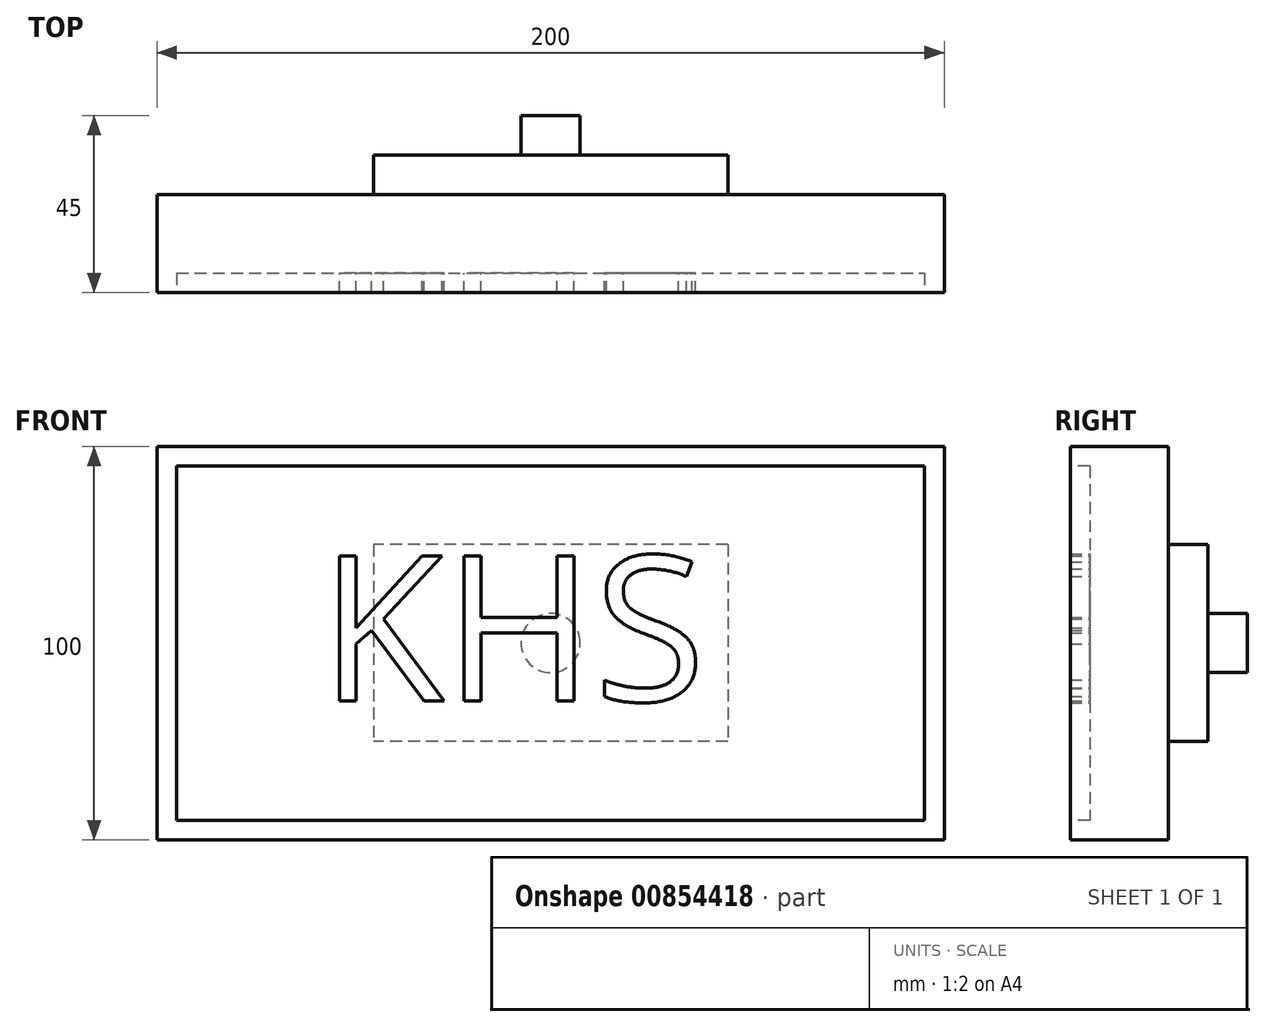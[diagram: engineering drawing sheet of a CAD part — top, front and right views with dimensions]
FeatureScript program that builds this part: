
annotation { "Feature Type Name" : "Feature", "Feature Type Description" : "" }
export const myFeature = defineFeature(function(context is Context, id is Id, definition is map)
    precondition{}
    {
        {
            var Q0;
            Q0=qCreatedBy(makeId("Front.planeOp"),FACE);
            var sketch = newSketch(context, id + "F0", { "sketchPlane" : qUnion([Q0])});
            skLineSegment(sketch, "E0.bottom", {"start": v(-100, 50) * mm, "end": v(100, 50) * mm});
            skLineSegment(sketch, "E0.top", {"start": v(-100, -50) * mm, "end": v(100, -50) * mm});
            skLineSegment(sketch, "E0.left", {"start": v(-100, 50) * mm, "end": v(-100, -50) * mm});
            skLineSegment(sketch, "E0.right", {"start": v(100, 50) * mm, "end": v(100, -50) * mm});
            skSolve(sketch);
        }
        {
            var Q0;
            Q0=makeQuery(id+"F0.imprint","IMPRINT",FACE,{"disambiguationData":[TD([[makeQuery(id+"F0.imprint","IMPRINT",EDGE,{"derivedFrom":sQuery(id+"F0.wireOp",EDGE,"E0.bottom")}),-1.0]])]});
            extrude(context, id + "F1", {"entities" : qUnion([Q0]), "depth" : 25 * mm, "offsetDistance" : 25 * mm});
        }
        {
            var Q0;
            Q0=makeQuery(id+"F1.opExtrude","CAP_FACE",FACE,{"disambiguationData":[OSD([sQuery(id+"F0.wireOp",EDGE,"E0.bottom"),sQuery(id+"F0.wireOp",EDGE,"E0.top"),sQuery(id+"F0.wireOp",EDGE,"E0.left"),sQuery(id+"F0.wireOp",EDGE,"E0.right")])],"isStart":false});
            var sketch = newSketch(context, id + "F2", { "sketchPlane" : qUnion([Q0])});
            skLineSegment(sketch, "E1.bottom", {"start": v(-95, 45) * mm, "end": v(95, 45) * mm});
            skLineSegment(sketch, "E1.top", {"start": v(-95, -45) * mm, "end": v(95, -45) * mm});
            skLineSegment(sketch, "E1.left", {"start": v(-95, 45) * mm, "end": v(-95, -45) * mm});
            skLineSegment(sketch, "E1.right", {"start": v(95, 45) * mm, "end": v(95, -45) * mm});
            skSolve(sketch);
        }
        {
            var Q0;
            Q0=makeQuery(id+"F2.imprint","IMPRINT",FACE,{"disambiguationData":[TD([[makeQuery(id+"F2.imprint","IMPRINT",EDGE,{"derivedFrom":sQuery(id+"F2.wireOp",EDGE,"E1.bottom")}),-1.0]])]});
            extrude(context, id + "F3", {"entities" : qUnion([Q0]), "operationType" : NewBodyOperationType.REMOVE, "oppositeDirection" : true, "depth" : 5 * mm, "offsetDistance" : 25 * mm});
        }
        {
            var Q0;
            Q0=makeQuery(id+"F1.opExtrude","CAP_FACE",FACE,{"disambiguationData":[OSD([sQuery(id+"F0.wireOp",EDGE,"E0.bottom"),sQuery(id+"F0.wireOp",EDGE,"E0.top"),sQuery(id+"F0.wireOp",EDGE,"E0.left"),sQuery(id+"F0.wireOp",EDGE,"E0.right")])],"isStart":true});
            var sketch = newSketch(context, id + "F4", { "sketchPlane" : qUnion([Q0])});
            skLineSegment(sketch, "E2.bottom", {"start": v(-45, 25) * mm, "end": v(45, 25) * mm});
            skLineSegment(sketch, "E2.top", {"start": v(-45, -25) * mm, "end": v(45, -25) * mm});
            skLineSegment(sketch, "E2.left", {"start": v(-45, 25) * mm, "end": v(-45, -25) * mm});
            skLineSegment(sketch, "E2.right", {"start": v(45, 25) * mm, "end": v(45, -25) * mm});
            skSolve(sketch);
        }
        {
            var Q0;
            Q0=makeQuery(id+"F4.imprint","IMPRINT",FACE,{"disambiguationData":[TD([[makeQuery(id+"F4.imprint","IMPRINT",EDGE,{"derivedFrom":sQuery(id+"F4.wireOp",EDGE,"E2.bottom")}),-1.0]])]});
            extrude(context, id + "F5", {"entities" : qUnion([Q0]), "operationType" : NewBodyOperationType.ADD, "depth" : 10 * mm, "offsetDistance" : 25 * mm});
        }
        {
            var Q0;
            Q0=makeQuery(id+"F5.opExtrude","CAP_FACE",FACE,{"disambiguationData":[OSD([sQuery(id+"F4.wireOp",EDGE,"E2.bottom"),sQuery(id+"F4.wireOp",EDGE,"E2.top"),sQuery(id+"F4.wireOp",EDGE,"E2.left"),sQuery(id+"F4.wireOp",EDGE,"E2.right")])],"isStart":false});
            var sketch = newSketch(context, id + "F6", { "sketchPlane" : qUnion([Q0])});
            skCircle(sketch, "E3", {"center": v(0, 0) * mm, "radius": 7.5 * mm});
            skSolve(sketch);
        }
        {
            var Q0;
            Q0=makeQuery(id+"F6.imprint","IMPRINT",FACE,{"disambiguationData":[TD([[makeQuery(id+"F6.imprint","IMPRINT",EDGE,{"derivedFrom":sQuery(id+"F6.wireOp",EDGE,"E3")}),1.0]])]});
            extrude(context, id + "F7", {"entities" : qUnion([Q0]), "operationType" : NewBodyOperationType.ADD, "depth" : 10 * mm, "offsetDistance" : 25 * mm});
        }
        {
            var Q0;
            Q0=makeQuery(id+"F3.boolean.opBoolean","COPY",FACE,{"derivedFrom":makeQuery(id+"F3.opExtrude","CAP_FACE",FACE,{"disambiguationData":[OSD([sQuery(id+"F2.wireOp",EDGE,"E1.bottom"),sQuery(id+"F2.wireOp",EDGE,"E1.top"),sQuery(id+"F2.wireOp",EDGE,"E1.left"),sQuery(id+"F2.wireOp",EDGE,"E1.right")])],"isStart":false})});
            var sketch = newSketch(context, id + "F8", { "sketchPlane" : qUnion([Q0])});
            skText(sketch, "E4", { "text": "KHS", "fontName": "OpenSans-Regular.ttf"});
            const initialGuessF8  = {"E4": [-0.05873, -0.01471, 1, 0, 0.03714]};
            skSetInitialGuess(sketch, initialGuessF8);
            skSolve(sketch);
        }
        {
            var Q0;
            Q0 = qSketchRegion(id + "F8", true);
            extrude(context, id + "F9", {"entities" : qUnion([Q0]), "operationType" : NewBodyOperationType.ADD, "depth" : 5 * mm, "offsetDistance" : 25 * mm});
        }
    });
